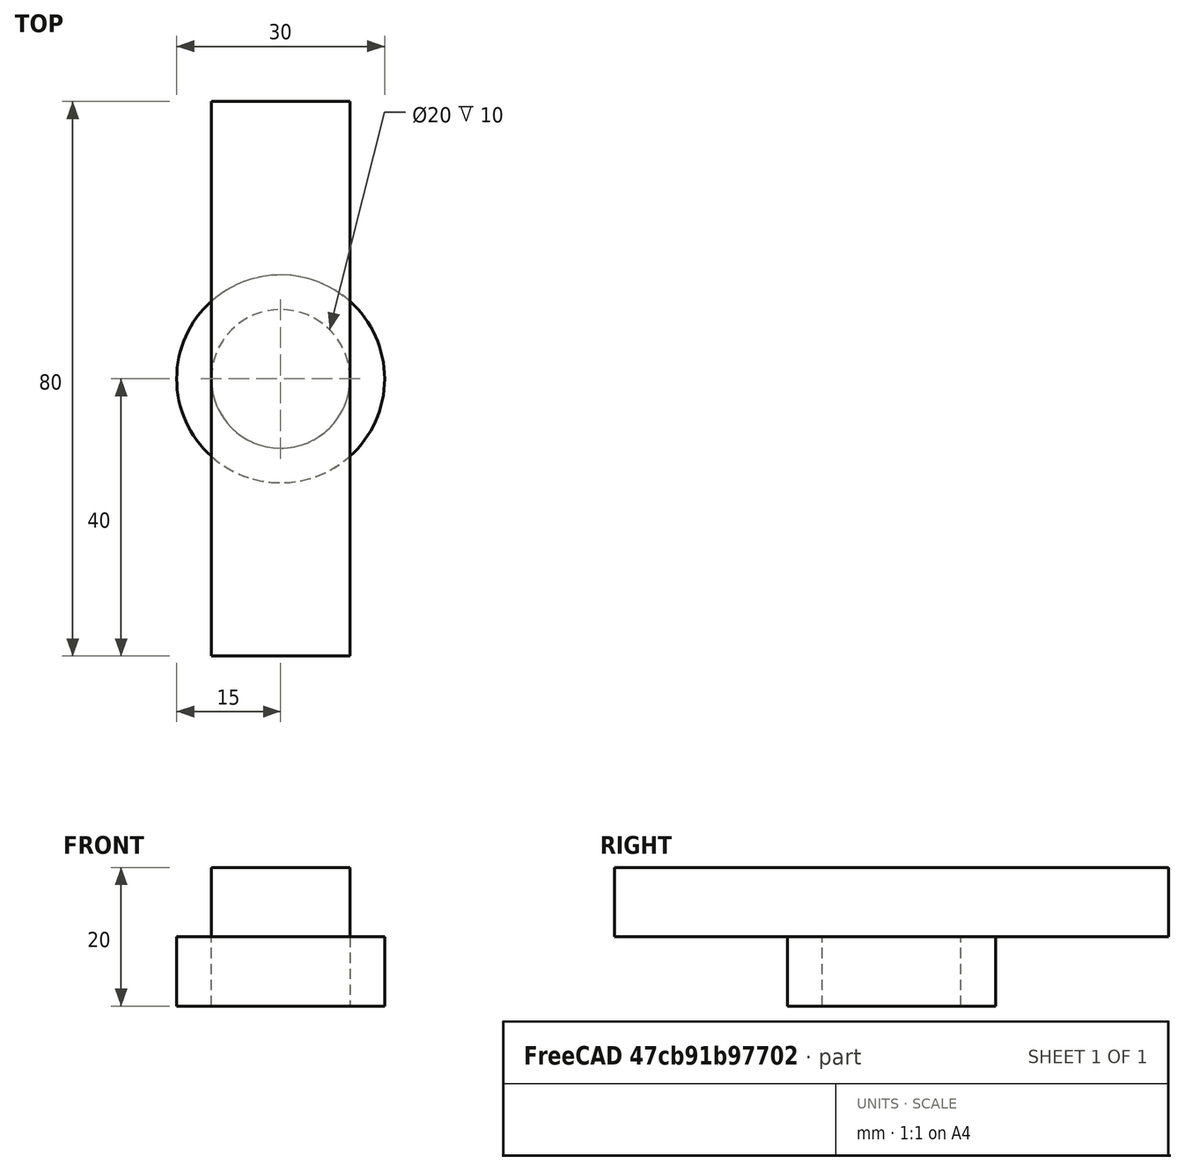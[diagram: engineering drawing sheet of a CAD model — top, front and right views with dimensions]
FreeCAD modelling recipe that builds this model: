
FCSTD DOCUMENT  (FreeCAD 0.20R29410 (Git))
Label: gp0
License: All rights reserved
LicenseURL: http://en.wikipedia.org/wiki/All_rights_reserved
objects: Sketcher::SketchObject×2, PartDesign::Pad×2, PartDesign::Body×1, Mesh::Feature×1
note: 7 computed .brp shape members not serialized (recipe doc carries the construction recipe); baked Part::Feature solids carry a one-line shape summary decoded from their .brp

FEATURE [Sketcher::SketchObject] Sketch
  FullyConstrained = true
  MapMode = 5
  Support = -> [XY_Plane]
  sketch-geometry (2):
    g0: Circle CenterX=0 CenterY=0 CenterZ=0 NormalX=0 NormalY=0 NormalZ=1 AngleXU=0 Radius=10
    g1: Circle CenterX=0 CenterY=0 CenterZ=0 NormalX=0 NormalY=0 NormalZ=1 AngleXU=0 Radius=15
  constraints (4):
    c: Coincident(g0,g-1)
    c: Coincident(g1,g0)
    c: Diameter(g0) = 20
    c: Diameter(g1) = 30
FEATURE [PartDesign::Pad] Pad
  Direction = (0,0,1)
  Length = 10
  Length2 = 100
  Profile = -> Sketch
  ReferenceAxis = -> Sketch [N_Axis]
  Reversed = true
  Type = 0
FEATURE [Sketcher::SketchObject] Sketch001
  FullyConstrained = true
  MapMode = 5
  Placement = pos=(0,0,0) rot=(1,0,0;1.5708rad)
  Support = -> [XZ_Plane]
  sketch-geometry (4):
    g0: LineSegment StartX=-10 StartY=0 StartZ=0 EndX=10 EndY=0 EndZ=0
    g1: LineSegment StartX=10 StartY=0 StartZ=0 EndX=10 EndY=10 EndZ=0
    g2: LineSegment StartX=10 StartY=10 StartZ=0 EndX=-10 EndY=10 EndZ=0
    g3: LineSegment StartX=-10 StartY=10 StartZ=0 EndX=-10 EndY=0 EndZ=0
  constraints (11):
    c: Coincident(g0,g1)
    c: Coincident(g1,g2)
    c: Coincident(g3,g0)
    c: Horizontal(g0)
    c: Horizontal(g2)
    c: Vertical(g1)
    c: Vertical(g3)
    c: DistanceY(g1,g1) = 10
    c: Symmetric(g0,g0,g-1)
    c: DistanceX(g3,g2) = 20
    c: Coincident(g2,g3)
FEATURE [PartDesign::Pad] Pad001
  BaseFeature = -> Pad
  Direction = (0,-1,-2e-16)
  Length = 80
  Length2 = 100
  Midplane = true
  Profile = -> Sketch001
  Type = 0
FEATURE [PartDesign::Body] Body
  Group = -> [Sketch,Pad,Sketch001,Pad001]
  Origin = -> Origin
  Tip = -> Pad001
FEATURE [Mesh::Feature] Mesh  label="Body (Meshed)"
